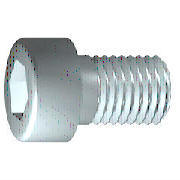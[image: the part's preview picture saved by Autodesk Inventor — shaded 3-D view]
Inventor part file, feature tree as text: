
AUTODESK INVENTOR PART (.ipt)
format: ipt  version: 2025 (Build 290162000, 162)  size: 187,904 bytes
history: native  units: mm (DEFAULTED — no unit token found)
features: extrude x1, plane x1, fillet x1
ambient origin geometry x7: Origin, YZ Plane, XY Plane, X Axis, Y Axis, Z Axis, Center Point
bodies: Solid1 (feature_tree), Body (feature_tree)
feature tree (3):
  extrude  "Slot"  Depth=16.0mm
  plane  "Work Plane1"
  fillet  "Fillet2"  Radius=0.24548mm
